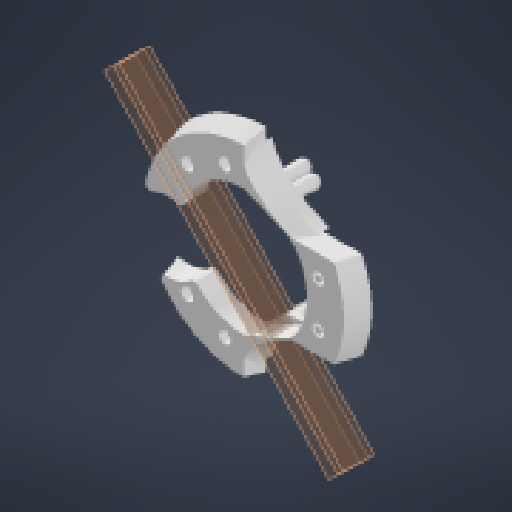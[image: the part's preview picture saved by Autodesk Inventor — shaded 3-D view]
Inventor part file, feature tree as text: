
AUTODESK INVENTOR PART (.ipt)
format: ipt  version: 2024 (Build 280153000, 153)  size: 601,600 bytes
history: native  units: in
note: dims shown in document units (in); Inventor stores cm internally (conversion verified against a paired STEP export)
features: sketch x7, other x6, chamfer x5, reference x5, extrude x4, plane x3, projected_geometry x3, sweep x2, mirror x1, fillet x1
ambient origin geometry x8: Origin, YZ Plane, XZ Plane, XY Plane, X Axis, Y Axis, Z Axis, Center Point
bodies: Solid1 (feature_tree)
feature tree (37):
  extrude  "Extrusion1"  Depth=0.125in TaperAngle=15.0deg
  chamfer  "Chamfer1"  Distance=0.125in Angle=15.0deg
  chamfer  "Chamfer2"  Distance=0.125in Angle=15.0deg
  chamfer  "Chamfer3"  Distance=0.1969in
  extrude  "Extrusion2"  Depth=0.125in
  extrude  "Extrusion3"  Depth=0.125in TaperAngle=0.0deg
  extrude  "Extrusion4"  Depth=0.125in
  plane  "Work Plane3"
  sketch  "Sketch5"  dims[d14=0.311in]
  sketch  "Sketch6"  dims[d15=0.311in]
  sketch  "Sketch7"  dims[d16=0.311in d17=0.1969in d18=0.0in d19=0.1969in d20=0.5512in d21=0.0in d22=0.0118in d23=0.1575in d24=0.0in d25=90.0deg d26=-0.1969in d27=-0.315in d28=0.3937in d30=0.315in d31=0.315in d32=0.0069in d33=0.0in d34=0.0069in d35=0.0in d36=0.3937in d37=0.125in d38=15.0deg d39=0.3937in d40=0.125in d41=15.0deg d42=0.125in]
  sweep  "Sweep1"
  sweep  "Sweep2"
  mirror  "Mirror1"
  chamfer  "Chamfer4"  [1 undecoded]
  chamfer  "Chamfer5"  Distance=0.3937in
  fillet  "Fillet1"  Radius=0.315in
  sketch  "Sketch1"  dims[d0=0.5512in d1=0.0in d2=0.5512in d3=0.125in d4=15.0deg d5=0.5512in d6=0.125in d7=15.0deg d8=0.5512in d9=0.125in d10=15.0deg]
  reference  "Reference1"
  reference  "Reference2"
  reference  "Reference3"
  sketch  "Sketch2"  dims[d11=0.311in]
  sketch  "Sketch3"  dims[d12=0.311in]
  reference  "Reference4"
  sketch  "Sketch4"  dims[d13=0.311in]
  reference  "Reference5"
  projected_geometry  "Projected Loop1"
  plane  "Work Plane1"
  plane  "Work Plane2"
  projected_geometry  "Projected Loop2"
  projected_geometry  "Projected Loop3"
  other  "<userpath>\Desktop\Camera_Mount.iam"
  other  "Camera_Mount.iam"
  other  "Spur Gears:2"
  other  "Spur Gear2:1"
  other  "Camera_Baseplate:1"
  other  "Spur Gear1:1"
note: 1 required parameter value undecoded (feature->parameter linkage not recoverable at this tier; creation-order binding heuristic only, values carry confidence <= 0.55)
